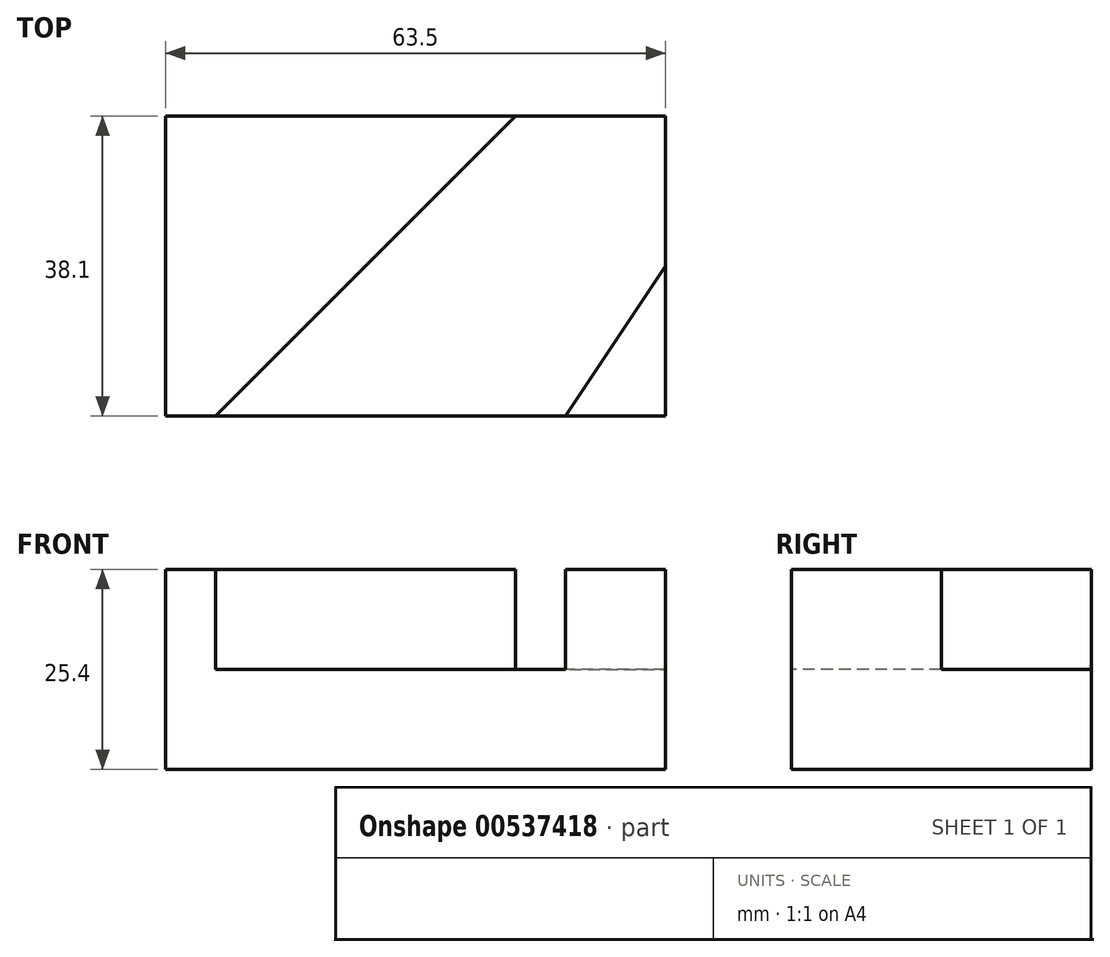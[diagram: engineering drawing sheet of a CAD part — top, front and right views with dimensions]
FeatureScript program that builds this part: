
annotation { "Feature Type Name" : "Feature", "Feature Type Description" : "" }
export const myFeature = defineFeature(function(context is Context, id is Id, definition is map)
    precondition{}
    {
        {
            var Q0;
            Q0=qCreatedBy(makeId("Right.planeOp"),FACE);
            var sketch = newSketch(context, id + "F0", { "sketchPlane" : qUnion([Q0])});
            skLineSegment(sketch, "E0", {"start": v(0, 0) * mm, "end": v(38.1, 0) * mm});
            skLineSegment(sketch, "E1", {"start": v(38.1, 0) * mm, "end": v(38.1, 25.4) * mm});
            skLineSegment(sketch, "E2", {"start": v(38.1, 25.4) * mm, "end": v(0, 25.4) * mm});
            skLineSegment(sketch, "E3", {"start": v(0, 25.4) * mm, "end": v(0, 0) * mm});
            skSolve(sketch);
        }
        {
            var Q0;
            Q0=makeQuery(id+"F0.imprint","IMPRINT",FACE,{"disambiguationData":[TD([[makeQuery(id+"F0.imprint","IMPRINT",EDGE,{"derivedFrom":sQuery(id+"F0.wireOp",EDGE,"E0")}),1.0]])]});
            extrude(context, id + "F1", {"entities" : qUnion([Q0]), "oppositeDirection" : true, "depth" : 63.5 * mm, "offsetDistance" : 25.4 * mm});
        }
        {
            var Q0;
            Q0=makeQuery(id+"F1.opExtrude","SWEPT_FACE",FACE,{"disambiguationData":[OSD([sQuery(id+"F0.wireOp",EDGE,"E3")])]});
            var sketch = newSketch(context, id + "F2", { "sketchPlane" : qUnion([Q0])});
            skLineSegment(sketch, "E4", {"start": v(-63.5, 12.7) * mm, "end": v(0, 12.7) * mm});
            skSolve(sketch);
        }
        {
            var Q0;
            Q0=makeQuery(id+"F1.opExtrude","CAP_FACE",FACE,{"disambiguationData":[OSD([sQuery(id+"F0.wireOp",EDGE,"E0"),sQuery(id+"F0.wireOp",EDGE,"E1"),sQuery(id+"F0.wireOp",EDGE,"E2"),sQuery(id+"F0.wireOp",EDGE,"E3")])],"isStart":true});
            var sketch = newSketch(context, id + "F3", { "sketchPlane" : qUnion([Q0])});
            skLineSegment(sketch, "E5", {"start": v(0, 12.7) * mm, "end": v(38.1, 12.7) * mm});
            skSolve(sketch);
        }
        {
            var Q0;
            Q0=makeQuery(id+"F1.opExtrude","SWEPT_FACE",FACE,{"disambiguationData":[OSD([sQuery(id+"F0.wireOp",EDGE,"E2")])]});
            var sketch = newSketch(context, id + "F4", { "sketchPlane" : qUnion([Q0])});
            skLineSegment(sketch, "E6", {"start": v(-63.5, 0) * mm, "end": v(-57.15, 0) * mm});
            skLineSegment(sketch, "E7", {"start": v(0, 38.1) * mm, "end": v(-19.05, 38.1) * mm});
            skLineSegment(sketch, "E8", {"start": v(-19.05, 38.1) * mm, "end": v(-57.15, 0) * mm});
            skLineSegment(sketch, "E9", {"start": v(0, 0) * mm, "end": v(-12.7, 0) * mm});
            skSolve(sketch);
        }
        {
            var Q0;
            {var subQ0=sQuery(id+"F3.wireOp",EDGE,"E5");Q0=makeQuery(id+"F3.imprint","IMPRINT",FACE,{"disambiguationData":[TD([[makeQuery(id+"F3.imprint","IMPRINT",EDGE,{"derivedFrom":subQ0}),1.0]])]});}
            var sketch = newSketch(context, id + "F5", { "sketchPlane" : qUnion([Q0])});
            skLineSegment(sketch, "E10", {"start": v(0, 12.7) * mm, "end": v(19.05, 12.7) * mm});
            skLineSegment(sketch, "E11", {"start": v(19.05, 12.7) * mm, "end": v(19.05, 25.4) * mm});
            skSolve(sketch);
        }
        {
            var Q0;
            Q0=makeQuery(id+"F4.imprint","IMPRINT",FACE,{"disambiguationData":[TD([[makeQuery(id+"F4.imprint","IMPRINT",EDGE,{"derivedFrom":sQuery(id+"F4.wireOp",EDGE,"E7")}),-1.0]])]});
            var sketch = newSketch(context, id + "F6", { "sketchPlane" : qUnion([Q0])});
            skLineSegment(sketch, "E12", {"start": v(0, 19.05) * mm, "end": v(-12.7, 0) * mm});
            skSolve(sketch);
        }
        {
            var Q0;
            {var subQ4=sQuery(id+"F6.wireOp",EDGE,"E12");Q0=makeQuery(id+"F6.imprint","IMPRINT",FACE,{"disambiguationData":[TD([[makeQuery(id+"F6.imprint","IMPRINT",EDGE,{"derivedFrom":subQ4}),-1.0]])]});}
            extrude(context, id + "F7", {"entities" : qUnion([Q0]), "operationType" : NewBodyOperationType.REMOVE, "oppositeDirection" : true, "depth" : 12.7 * mm, "offsetDistance" : 25.4 * mm});
        }
    });
